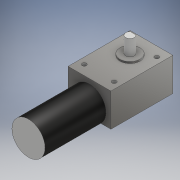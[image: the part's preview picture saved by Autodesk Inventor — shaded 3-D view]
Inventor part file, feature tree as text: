
AUTODESK INVENTOR PART (.ipt)
format: ipt  version: 2017 (Build 210142000, 142)  size: 176,640 bytes
history: native  units: mm
features: extrude x6, sketch x6, projected_geometry x2, plane x1, mirror x1
ambient origin geometry x8: Origin, YZ Plane, XZ Plane, XY Plane, X Axis, Y Axis, Z Axis, Center Point
bodies: Solid1 (feature_tree)
feature tree (16):
  extrude  "Extrusion1"  Depth=58.1mm
  extrude  "Extrusion2"  Depth=31.0mm
  extrude  "Extrusion3"  Depth=1.5mm TaperAngle=0.0deg
  extrude  "Extrusion4"  Depth=14.9mm TaperAngle=0.0deg
  extrude  "Extrusion5"  Depth=12.0mm TaperAngle=0.0deg
  plane  "Work Plane1"
  mirror  "Mirror1"
  extrude  "Extrusion6"  Depth=57.2mm
  sketch  "Sketch1"  dims[d0=40.12mm d1=58.1mm]
  sketch  "Sketch2"  dims[d2=31.0mm d3=0.0mm d4=18.8mm]
  sketch  "Sketch3"  dims[d5=37.9mm d6=1.5mm d7=0.0mm]
  projected_geometry  "Projected Loop1"
  sketch  "Sketch4"  dims[d8=8.0mm d9=14.9mm d10=0.0mm]
  sketch  "Sketch5"  dims[d11=7.0mm d12=12.0mm d13=0.0mm]
  projected_geometry  "Projected Loop2"
  sketch  "Sketch6"  dims[d14=28.0mm d15=40.0mm d16=4.0mm d17=6.0mm d18=0.0mm d19=31.0mm d20=4.2mm d21=57.2mm d22=0.0mm]
